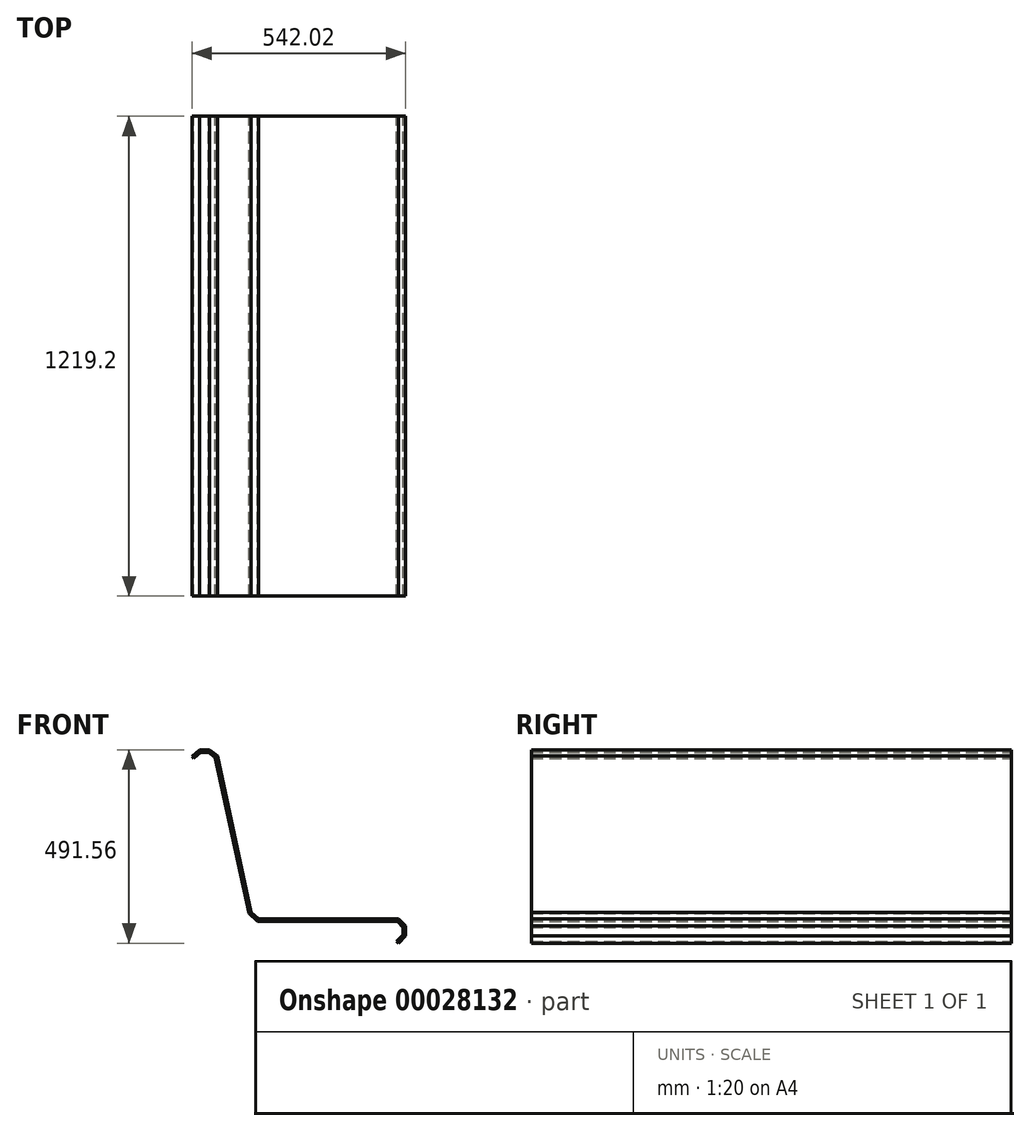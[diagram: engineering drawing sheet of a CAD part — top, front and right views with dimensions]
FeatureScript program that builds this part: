
annotation { "Feature Type Name" : "Feature", "Feature Type Description" : "" }
export const myFeature = defineFeature(function(context is Context, id is Id, definition is map)
    precondition{}
    {
        {
            var Q0;
            Q0=qCreatedBy(makeId("Front.planeOp"),FACE);
            var sketch = newSketch(context, id + "F0", { "sketchPlane" : qUnion([Q0])});
            skLineSegment(sketch, "E0", {"start": v(-210.92, 170.1) * mm, "end": v(-192.13, 187.18) * mm});
            skLineSegment(sketch, "E1", {"start": v(-192.13, 187.18) * mm, "end": v(-166.73, 187.18) * mm});
            skLineSegment(sketch, "E2", {"start": v(-166.73, 187.18) * mm, "end": v(-146.76, 171.49) * mm});
            skLineSegment(sketch, "E3", {"start": v(-146.76, 171.49) * mm, "end": v(-61.07, -225.78) * mm});
            skLineSegment(sketch, "E4", {"start": v(-61.07, -225.78) * mm, "end": v(-42.46, -243.06) * mm});
            skLineSegment(sketch, "E5", {"start": v(-42.46, -243.06) * mm, "end": v(313.14, -243.06) * mm});
            skLineSegment(sketch, "E6", {"start": v(313.14, -243.06) * mm, "end": v(331.1, -261.02) * mm});
            skLineSegment(sketch, "E7", {"start": v(331.1, -261.02) * mm, "end": v(331.1, -286.42) * mm});
            skLineSegment(sketch, "E8", {"start": v(331.1, -286.42) * mm, "end": v(313.14, -304.38) * mm});
            skLineSegment(sketch, "E9.0", {"start": v(324.75, -283.8) * mm, "end": v(308.65, -299.9) * mm});
            skLineSegment(sketch, "E9.1", {"start": v(324.75, -263.65) * mm, "end": v(324.75, -283.8) * mm});
            skLineSegment(sketch, "E9.2", {"start": v(310.51, -249.41) * mm, "end": v(324.75, -263.65) * mm});
            skLineSegment(sketch, "E9.3", {"start": v(-44.95, -249.41) * mm, "end": v(310.51, -249.41) * mm});
            skLineSegment(sketch, "E9.4", {"start": v(-66.86, -229.07) * mm, "end": v(-44.95, -249.41) * mm});
            skLineSegment(sketch, "E9.5", {"start": v(-152.48, 167.9) * mm, "end": v(-66.86, -229.07) * mm});
            skLineSegment(sketch, "E9.6", {"start": v(-168.93, 180.83) * mm, "end": v(-152.48, 167.9) * mm});
            skLineSegment(sketch, "E9.7", {"start": v(-189.67, 180.83) * mm, "end": v(-168.93, 180.83) * mm});
            skLineSegment(sketch, "E9.8", {"start": v(-206.65, 165.4) * mm, "end": v(-189.67, 180.83) * mm});
            skLineSegment(sketch, "E10", {"start": v(-210.92, 170.1) * mm, "end": v(-206.65, 165.4) * mm});
            skLineSegment(sketch, "E11", {"start": v(313.14, -304.38) * mm, "end": v(308.65, -299.9) * mm});
            skSolve(sketch);
        }
        {
            var Q0;
            Q0=makeQuery(id+"F0.imprint","IMPRINT",FACE,{"disambiguationData":[TD([[makeQuery(id+"F0.imprint","IMPRINT",EDGE,{"derivedFrom":sQuery(id+"F0.wireOp",EDGE,"E0")}),-1.0]])]});
            extrude(context, id + "F1", {"entities" : qUnion([Q0]), "depth" : 1219.2 * mm});
        }
    });
